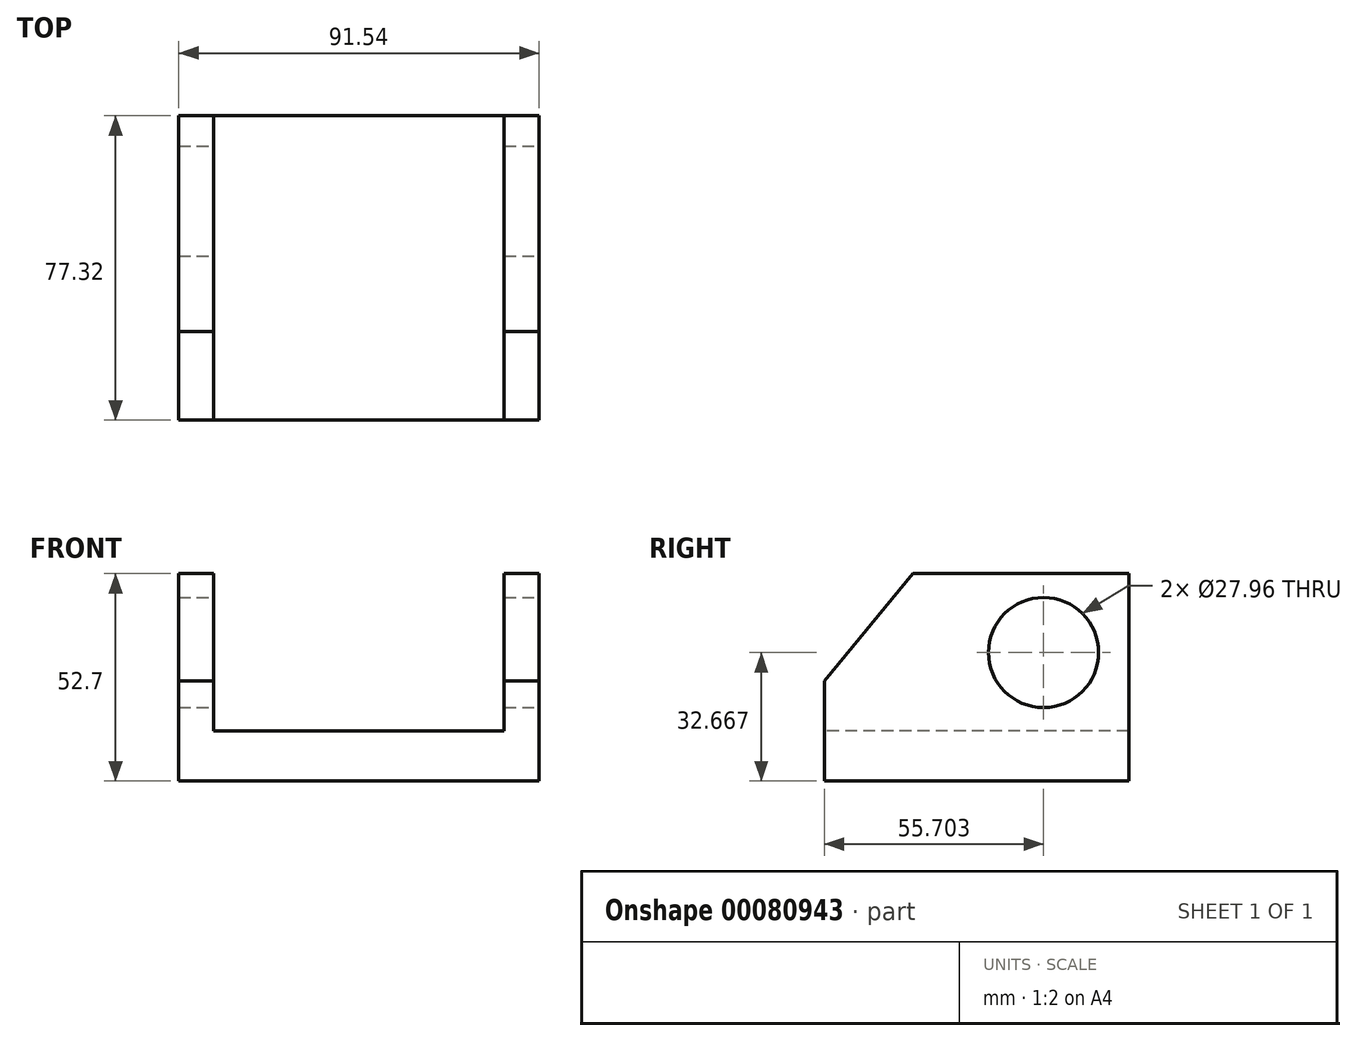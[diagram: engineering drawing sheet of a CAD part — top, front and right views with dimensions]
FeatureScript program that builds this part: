
annotation { "Feature Type Name" : "Feature", "Feature Type Description" : "" }
export const myFeature = defineFeature(function(context is Context, id is Id, definition is map)
    precondition{}
    {
        {
            var Q0;
            Q0=qCreatedBy(makeId("Top.planeOp"),FACE);
            var sketch = newSketch(context, id + "F0", { "sketchPlane" : qUnion([Q0])});
            skLineSegment(sketch, "E0", {"start": v(-45.77, 0) * mm, "end": v(-45.77, 38.66) * mm});
            skLineSegment(sketch, "E1", {"start": v(-45.77, 38.66) * mm, "end": v(0, 38.66) * mm});
            skLineSegment(sketch, "E2.MirrorCS", {"start": v(45.77, 38.66) * mm, "end": v(0, 38.66) * mm});
            skLineSegment(sketch, "E3.MirrorCS", {"start": v(45.77, 0) * mm, "end": v(45.77, 38.66) * mm});
            skLineSegment(sketch, "E4.MirrorCS", {"start": v(-45.77, 0) * mm, "end": v(-45.77, -38.66) * mm});
            skLineSegment(sketch, "E5.MirrorCS", {"start": v(-45.77, -38.66) * mm, "end": v(0, -38.66) * mm});
            skLineSegment(sketch, "E6.MirrorCS", {"start": v(45.77, -38.66) * mm, "end": v(0, -38.66) * mm});
            skLineSegment(sketch, "E7.MirrorCS", {"start": v(45.77, 0) * mm, "end": v(45.77, -38.66) * mm});
            skSolve(sketch);
        }
        {
            var Q0;
            Q0 = qSketchRegion(id + "F0", true);
            extrude(context, id + "F1", {"entities" : qUnion([Q0]), "depth" : 12.7 * mm});
        }
        {
            var Q0;
            Q0=makeQuery(id+"F1.opExtrude","CAP_FACE",FACE,{"disambiguationData":[OSD([sQuery(id+"F0.wireOp",EDGE,"E0"),sQuery(id+"F0.wireOp",EDGE,"E1"),sQuery(id+"F0.wireOp",EDGE,"E2.MirrorCS"),sQuery(id+"F0.wireOp",EDGE,"E3.MirrorCS"),sQuery(id+"F0.wireOp",EDGE,"E4.MirrorCS"),sQuery(id+"F0.wireOp",EDGE,"E5.MirrorCS"),sQuery(id+"F0.wireOp",EDGE,"E6.MirrorCS"),sQuery(id+"F0.wireOp",EDGE,"E7.MirrorCS")])],"isStart":false});
            var sketch = newSketch(context, id + "F2", { "sketchPlane" : qUnion([Q0])});
            skLineSegment(sketch, "E8", {"start": v(36.93, 38.66) * mm, "end": v(36.93, -38.66) * mm});
            skLineSegment(sketch, "E9", {"start": v(36.93, -38.66) * mm, "end": v(45.77, -38.66) * mm});
            skLineSegment(sketch, "E10", {"start": v(45.77, -38.66) * mm, "end": v(45.77, 38.66) * mm});
            skLineSegment(sketch, "E11", {"start": v(45.77, 38.66) * mm, "end": v(36.93, 38.66) * mm});
            skLineSegment(sketch, "E12.MirrorCS", {"start": v(-36.93, 38.66) * mm, "end": v(-36.93, -38.66) * mm});
            skLineSegment(sketch, "E13.MirrorCS", {"start": v(-45.77, -38.66) * mm, "end": v(-45.77, 38.66) * mm});
            skLineSegment(sketch, "E14.MirrorCS", {"start": v(-45.77, 38.66) * mm, "end": v(-36.93, 38.66) * mm});
            skLineSegment(sketch, "E15.MirrorCS", {"start": v(-36.93, -38.66) * mm, "end": v(-45.77, -38.66) * mm});
            skSolve(sketch);
        }
        {
            var Q0;
            Q0 = qSketchRegion(id + "F2", true);
            extrude(context, id + "F3", {"entities" : qUnion([Q0]), "operationType" : NewBodyOperationType.ADD, "depth" : 40 * mm});
        }
        {
            var Q0;
            Q0=makeQuery(id+"F3.boolean.opBoolean","MERGE",FACE,{"derivedFrom":[makeQuery(id+"F1.opExtrude","SWEPT_FACE",FACE,{"disambiguationData":[OSD([sQuery(id+"F0.wireOp",EDGE,"E3.MirrorCS"),sQuery(id+"F0.wireOp",EDGE,"E7.MirrorCS")])]}),makeQuery(id+"F3.opExtrude","SWEPT_FACE",FACE,{"disambiguationData":[OSD([sQuery(id+"F2.wireOp",EDGE,"E10")])]})]});
            var sketch = newSketch(context, id + "F4", { "sketchPlane" : qUnion([Q0])});
            skLineSegment(sketch, "E16", {"start": v(-38.66, 25.4) * mm, "end": v(-16.1, 52.7) * mm});
            skLineSegment(sketch, "E17", {"start": v(-16.1, 52.7) * mm, "end": v(-38.66, 52.7) * mm});
            skLineSegment(sketch, "E18", {"start": v(-38.66, 52.7) * mm, "end": v(-38.66, 25.4) * mm});
            skCircle(sketch, "E19", {"center": v(17.04, 32.67) * mm, "radius": 13.98 * mm});
            skSolve(sketch);
        }
        {
            var Q0;
            Q0 = qSketchRegion(id + "F4", true);
            extrude(context, id + "F5", {"entities" : qUnion([Q0]), "operationType" : NewBodyOperationType.REMOVE, "endBound" : BoundingType.THROUGH_ALL, "oppositeDirection" : true, "depth" : 25.4 * mm});
        }
    });
